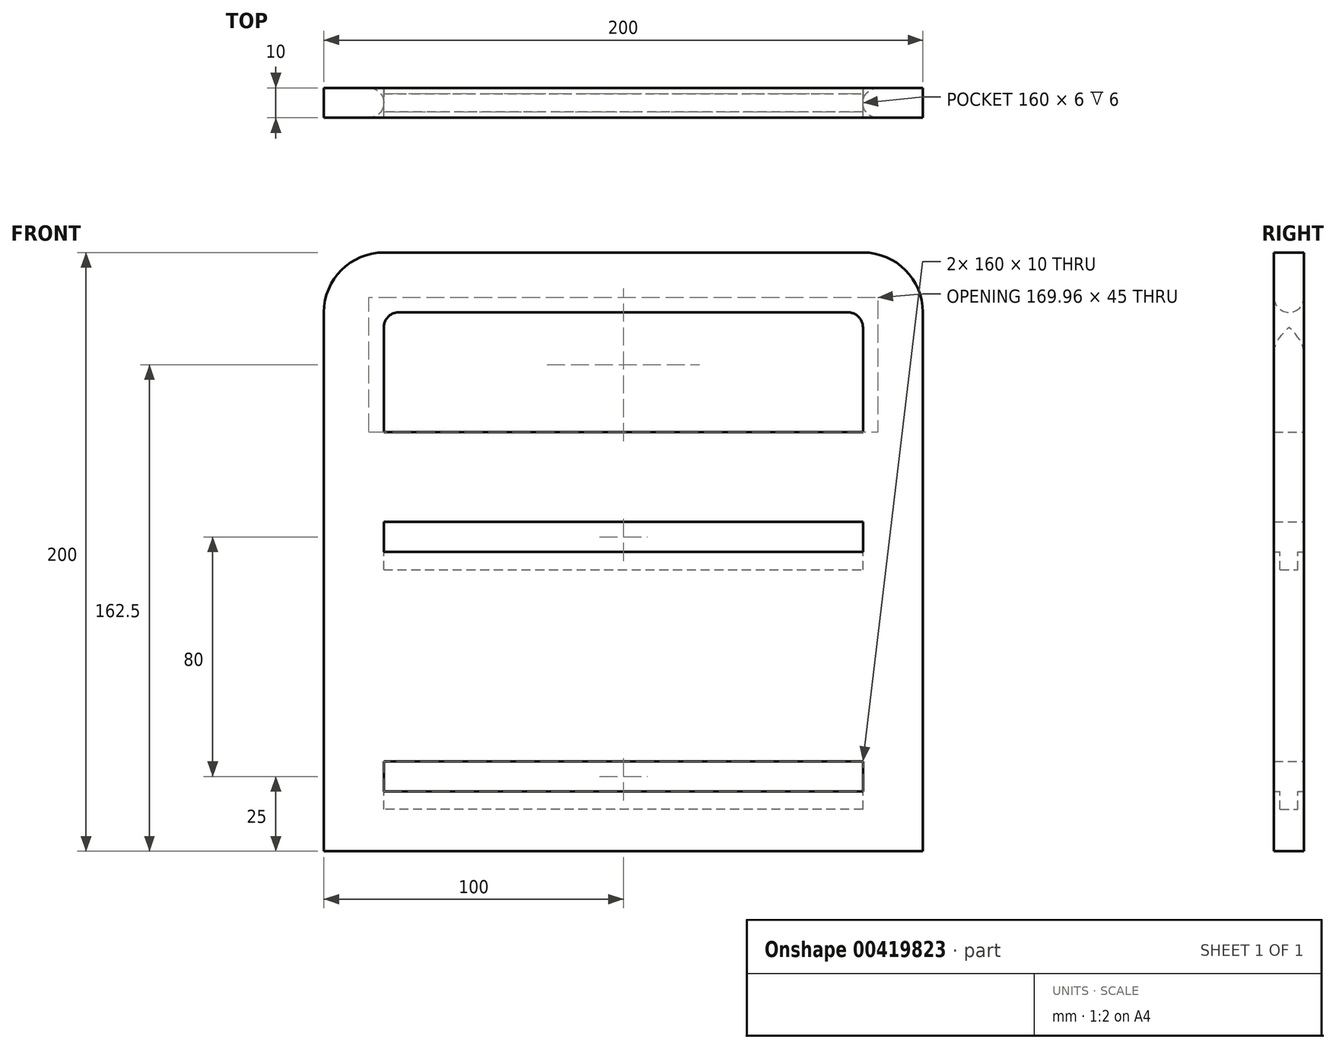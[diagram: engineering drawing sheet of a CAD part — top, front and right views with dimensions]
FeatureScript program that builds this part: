
annotation { "Feature Type Name" : "Feature", "Feature Type Description" : "" }
export const myFeature = defineFeature(function(context is Context, id is Id, definition is map)
    precondition{}
    {
        {
            var Q0;
            Q0=qCreatedBy(makeId("Front.planeOp"),FACE);
            var sketch = newSketch(context, id + "F0", { "sketchPlane" : qUnion([Q0])});
            skLineSegment(sketch, "E0.bottom", {"start": v(0, 0) * mm, "end": v(100, 0) * mm});
            skLineSegment(sketch, "E0.top", {"start": v(0, 200) * mm, "end": v(100, 200) * mm});
            skLineSegment(sketch, "E0.left", {"start": v(0, 0) * mm, "end": v(0, 200) * mm, "construction": true});
            skLineSegment(sketch, "E0.right", {"start": v(100, 0) * mm, "end": v(100, 200) * mm});
            skLineSegment(sketch, "E1.MirrorCS", {"start": v(0, 0) * mm, "end": v(-100, 0) * mm});
            skLineSegment(sketch, "E2.MirrorCS", {"start": v(-100, 0) * mm, "end": v(-100, 200) * mm});
            skLineSegment(sketch, "E3.MirrorCS", {"start": v(0, 200) * mm, "end": v(-100, 200) * mm});
            skLineSegment(sketch, "E4.bottom", {"start": v(80, 140) * mm, "end": v(-80, 140) * mm});
            skLineSegment(sketch, "E4.top", {"start": v(80, 180) * mm, "end": v(-80, 180) * mm});
            skLineSegment(sketch, "E4.left", {"start": v(80, 140) * mm, "end": v(80, 180) * mm});
            skLineSegment(sketch, "E4.right", {"start": v(-80, 140) * mm, "end": v(-80, 180) * mm});
            skPoint(sketch, "E4.middle", {"position": v(0, 160) * mm});
            skLineSegment(sketch, "E5.bottom", {"start": v(-80, 20) * mm, "end": v(80, 20) * mm});
            skLineSegment(sketch, "E5.top", {"start": v(-80, 30) * mm, "end": v(80, 30) * mm});
            skLineSegment(sketch, "E5.left", {"start": v(-80, 20) * mm, "end": v(-80, 30) * mm});
            skLineSegment(sketch, "E5.right", {"start": v(80, 20) * mm, "end": v(80, 30) * mm});
            skPoint(sketch, "E5.middle", {"position": v(0, 25) * mm});
            skLineSegment(sketch, "E6.bottom", {"start": v(-80, 100) * mm, "end": v(80, 100) * mm});
            skLineSegment(sketch, "E6.top", {"start": v(-80, 110) * mm, "end": v(80, 110) * mm});
            skLineSegment(sketch, "E6.left", {"start": v(-80, 100) * mm, "end": v(-80, 110) * mm});
            skLineSegment(sketch, "E6.right", {"start": v(80, 100) * mm, "end": v(80, 110) * mm});
            skPoint(sketch, "E6.middle", {"position": v(0, 105) * mm});
            skSolve(sketch);
        }
        {
            var Q0;
            Q0=makeQuery(id+"F0.imprint","IMPRINT",FACE,{"disambiguationData":[TD([[makeQuery(id+"F0.imprint","IMPRINT",EDGE,{"derivedFrom":sQuery(id+"F0.wireOp",EDGE,"E0.bottom")}),1.0]])]});
            extrude(context, id + "F1", {"entities" : qUnion([Q0]), "depth" : 5 * mm, "hasSecondDirection" : true, "secondDirectionOppositeDirection" : true, "secondDirectionDepth" : 5 * mm});
        }
        {
            var Q0;
            Q0=makeQuery(id+"F1.opExtrude","SWEPT_FACE",FACE,{"disambiguationData":[OSD([sQuery(id+"F0.wireOp",EDGE,"E4.top")])]});
            fillet(context, id + "F2", {"entities" : qUnion([Q0]), "radius" : 5 * mm, "tangentPropagation" : true, "allowEdgeOverflow" : false});
        }
        {
            var Q0;
            Q0=makeQuery(id+"F1.opExtrude","SWEPT_EDGE",EDGE,{"disambiguationData":[OSD([sQuery(id+"F0.wireOp",EDGE,"E2.MirrorCS"),sQuery(id+"F0.wireOp",EDGE,"E3.MirrorCS")])]});
            var Q1;
            Q1=makeQuery(id+"F1.opExtrude","SWEPT_EDGE",EDGE,{"disambiguationData":[OSD([sQuery(id+"F0.wireOp",EDGE,"E0.top"),sQuery(id+"F0.wireOp",EDGE,"E0.right")])]});
            fillet(context, id + "F3", {"entities" : qUnion([Q0, Q1]), "radius" : 20 * mm, "tangentPropagation" : true, "allowEdgeOverflow" : false});
        }
        {
            var Q0;
            Q0=makeQuery(id+"F1.opExtrude","SWEPT_FACE",FACE,{"disambiguationData":[OSD([sQuery(id+"F0.wireOp",EDGE,"E5.bottom")])]});
            var sketch = newSketch(context, id + "F4", { "sketchPlane" : qUnion([Q0])});
            skLineSegment(sketch, "E7.bottom", {"start": v(80, -3) * mm, "end": v(-80, -3) * mm});
            skLineSegment(sketch, "E7.top", {"start": v(80, 3) * mm, "end": v(-80, 3) * mm});
            skLineSegment(sketch, "E7.left", {"start": v(80, -3) * mm, "end": v(80, 3) * mm});
            skLineSegment(sketch, "E7.right", {"start": v(-80, -3) * mm, "end": v(-80, 3) * mm});
            skPoint(sketch, "E7.middle", {"position": v(0, 0) * mm});
            skSolve(sketch);
        }
        {
            var Q0;
            Q0=makeQuery(id+"F4.imprint","IMPRINT",FACE,{"disambiguationData":[TD([[makeQuery(id+"F4.imprint","IMPRINT",EDGE,{"derivedFrom":sQuery(id+"F4.wireOp",EDGE,"E7.bottom")}),-1.0]])]});
            extrude(context, id + "F5", {"entities" : qUnion([Q0]), "operationType" : NewBodyOperationType.REMOVE, "oppositeDirection" : true, "depth" : 6 * mm});
        }
        {
            var Q0;
            Q0=makeQuery(id+"F1.opExtrude","SWEPT_FACE",FACE,{"disambiguationData":[OSD([sQuery(id+"F0.wireOp",EDGE,"E6.bottom")])]});
            var sketch = newSketch(context, id + "F6", { "sketchPlane" : qUnion([Q0])});
            skLineSegment(sketch, "E8.bottom", {"start": v(-80, -3) * mm, "end": v(80, -3) * mm});
            skLineSegment(sketch, "E8.top", {"start": v(-80, 3) * mm, "end": v(80, 3) * mm});
            skLineSegment(sketch, "E8.left", {"start": v(-80, -3) * mm, "end": v(-80, 3) * mm});
            skLineSegment(sketch, "E8.right", {"start": v(80, -3) * mm, "end": v(80, 3) * mm});
            skPoint(sketch, "E8.middle", {"position": v(0, 0) * mm});
            skSolve(sketch);
        }
        {
            var Q0;
            Q0=makeQuery(id+"F6.imprint","IMPRINT",FACE,{"disambiguationData":[TD([[makeQuery(id+"F6.imprint","IMPRINT",EDGE,{"derivedFrom":sQuery(id+"F6.wireOp",EDGE,"E8.bottom")}),1.0]])]});
            extrude(context, id + "F7", {"entities" : qUnion([Q0]), "operationType" : NewBodyOperationType.REMOVE, "oppositeDirection" : true, "depth" : 6 * mm});
        }
    });
